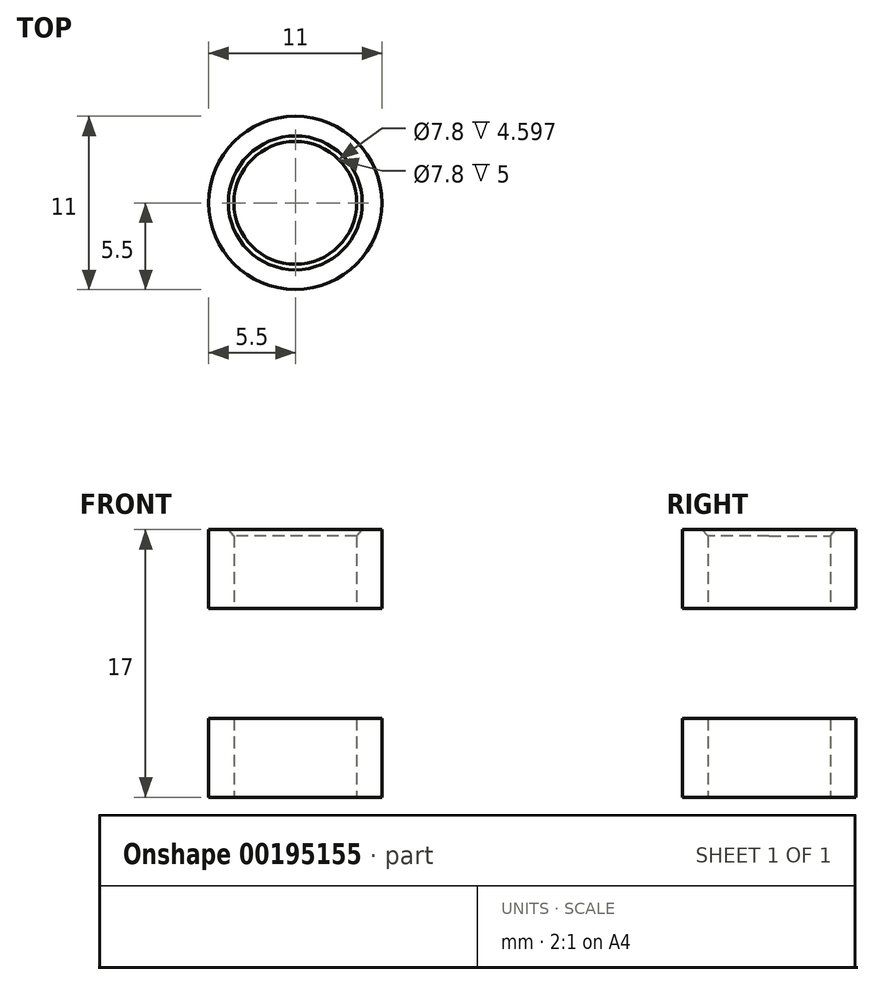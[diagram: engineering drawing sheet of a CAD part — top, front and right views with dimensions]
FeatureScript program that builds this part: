
annotation { "Feature Type Name" : "Feature", "Feature Type Description" : "" }
export const myFeature = defineFeature(function(context is Context, id is Id, definition is map)
    precondition{}
    {
        {
            var Q0;
            Q0=qCreatedBy(makeId("Top.planeOp"),FACE);
            var sketch = newSketch(context, id + "F0", { "sketchPlane" : qUnion([Q0])});
            skCircle(sketch, "E0", {"center": v(0, 0) * mm, "radius": 5.5 * mm});
            skSolve(sketch);
        }
        {
            var Q0;
            Q0=makeQuery(id+"F0.imprint","IMPRINT",FACE,{"disambiguationData":[TD([[makeQuery(id+"F0.imprint","IMPRINT",EDGE,{"derivedFrom":sQuery(id+"F0.wireOp",EDGE,"E0")}),1.0]])]});
            extrude(context, id + "F1", {"entities" : qUnion([Q0]), "depth" : 17 * mm});
        }
        {
            var Q0;
            Q0=makeQuery(id+"F1.opExtrude","CAP_FACE",FACE,{"disambiguationData":[OSD([sQuery(id+"F0.wireOp",EDGE,"E0")])],"isStart":true});
            cPlane(context, id + "F2", {"entities" : qUnion([Q0]), "cplaneType" : CPlaneType.OFFSET, "offset" : 5 * mm, "oppositeDirection" : true, "width" : 150 * mm, "height" : 150 * mm});
        }
        {
            var Q0;
            Q0=qCreatedBy(id+"F2.planeOp",FACE);
            var sketch = newSketch(context, id + "F3", { "sketchPlane" : qUnion([Q0])});
            skCircle(sketch, "E1", {"center": v(0, 0) * mm, "radius": 3.9 * mm});
            skCircle(sketch, "E2.0", {"center": v(0, 0) * mm, "radius": 5.5 * mm});
            skSolve(sketch);
        }
        {
            var Q0;
            Q0 = qSketchRegion(id + "F3", true);
            extrude(context, id + "F4", {"entities" : qUnion([Q0]), "operationType" : NewBodyOperationType.REMOVE, "oppositeDirection" : true, "depth" : 7 * mm});
        }
        {
            var Q0;
            Q0=makeQuery(id+"F1.opExtrude","CAP_FACE",FACE,{"disambiguationData":[OSD([sQuery(id+"F0.wireOp",EDGE,"E0")])],"isStart":false});
            cPlane(context, id + "F5", {"entities" : qUnion([Q0]), "cplaneType" : CPlaneType.OFFSET, "offset" : 8.5 * mm, "oppositeDirection" : true, "width" : 150 * mm, "height" : 150 * mm});
        }
        {
            var Q0;
            Q0=qCreatedBy(id+"F5.planeOp",FACE);
            var sketch = newSketch(context, id + "F6", { "sketchPlane" : qUnion([Q0])});
            skCircle(sketch, "E3.0", {"center": v(0, 0) * mm, "radius": 3.9 * mm});
            skSolve(sketch);
        }
        {
            var Q0;
            Q0 = qSketchRegion(id + "F6", true);
            extrude(context, id + "F7", {"entities" : qUnion([Q0]), "operationType" : NewBodyOperationType.REMOVE, "depth" : .1 * mm});
        }
        {
            var Q0;
            Q0=makeQuery(id+"F1.opExtrude","CAP_FACE",FACE,{"disambiguationData":[OSD([sQuery(id+"F0.wireOp",EDGE,"E0")])],"isStart":false});
            var sketch = newSketch(context, id + "F8", { "sketchPlane" : qUnion([Q0])});
            skCircle(sketch, "E4", {"center": v(0, 0) * mm, "radius": 2.25 * mm});
            skSolve(sketch);
        }
        {
            var Q0;
            Q0=sQuery(id+"F8.wireOp",VERTEX,"E4.center");
            var Q1;
            Q1=makeQuery(id+"F7.boolean.opBoolean","SPLIT",BODY,{"disambiguationData":[OD(0.0)],"derivedFrom":makeQuery(id+"F1.opExtrude","SWEPT_BODY",BODY,{"disambiguationData":[OSD([sQuery(id+"F0.wireOp",EDGE,"E0")])]})});
            var Q2;
            Q2=makeQuery(id+"F7.boolean.opBoolean","SPLIT",BODY,{"disambiguationData":[OD(1.0)],"derivedFrom":makeQuery(id+"F1.opExtrude","SWEPT_BODY",BODY,{"disambiguationData":[OSD([sQuery(id+"F0.wireOp",EDGE,"E0")])]})});
            hole(context, id + "F9", {"style" : HoleStyle.C_SINK, "endStyle" : HoleEndStyle.THROUGH, "holeDiameter" : 4.5 * mm, "cSinkDiameter" : 8.5 * mm, "cSinkAngle" : 82 * degree, "locations" : qUnion([Q0]), "scope" : qUnion([Q1, Q2]), "isTappedThrough" : true});
        }
        {
            var Q0;
            Q0=makeQuery(id+"F1.opExtrude","CAP_FACE",FACE,{"disambiguationData":[OSD([sQuery(id+"F0.wireOp",EDGE,"E0")])],"isStart":true});
            var sketch = newSketch(context, id + "F10", { "sketchPlane" : qUnion([Q0])});
            skCircle(sketch, "E5", {"center": v(0, 0) * mm, "radius": 3.9 * mm});
            skSolve(sketch);
        }
        {
            var Q0;
            Q0=makeQuery(id+"F10.imprint","IMPRINT",FACE,{"disambiguationData":[TD([[makeQuery(id+"F10.imprint","IMPRINT",EDGE,{"derivedFrom":sQuery(id+"F10.wireOp",EDGE,"E5")}),1.0]])]});
            extrude(context, id + "F11", {"entities" : qUnion([Q0]), "operationType" : NewBodyOperationType.REMOVE, "endBound" : BoundingType.THROUGH_ALL, "oppositeDirection" : true, "depth" : 25 * mm});
        }
    });
